# Revit family: Appliance_Cabinet-Danver-Grill_Base-Caliber_Rockwell
name_source: partatom
category: Casework
units: mm (PartAtom-declared; Revit-internal decimal feet)

## family parameters
Always vertical = Yes
Classification Number = 23.40.35.17.47
Cut with Voids When Loaded = No
Room Calculation Point = No
Shared = No
Work Plane-Based = No

## types (2) — shared parameters
Cabinet Material = Metal - Danver - Stainless Steel
Construction Type = 304 Grade Stainless Steel
Default Elevation = 0' - 0"
Depth = 2' - 3"
Depth+Door = 2' - 3 7/8"
Grill Box Depth = 1' - 5"
Handle Material = Metal - Danver - Chrome Plated Steel
Height = 2' - 6"
Keynote = 12 35 28
Manufacturer = Danver Outdoor Kitchens
Product Documentation Link = https://danver.com
Product Name = Appliance Cabinet - Danver  - Grill Base - Caliber Rockwell
Product Page URL = https://danver.com
Toe Height = 0' - 4 1/2"
Toe Kick Material = Metal - Danver - Toe Kick
URL = www.danver.com
Version = 2019 - V1.0b

## per-type parameters (varying)
| type | Constraints | Description | Model | Width |
| 42" Width - 2 Drawers - 0 Doors - Caliber Rockwell | 1 | 42in x27in D Grill Base - 2 Drawers Custom Deep Shelf for Hasty Bake | OGB4220-HB | 3' - 6" |
| 48" Width - 2 Drawers - 0 Doors - Caliber Rockwell | 2 | 48in x27in D Grill Base - 2 Drawers Custom Deep Shelf for Hasty Bake | OGB4820-HB | 4' - 0" |

## geometry (parser evidence)
native form markers: Sweep x16
no freeform markers — native parametric forms only
